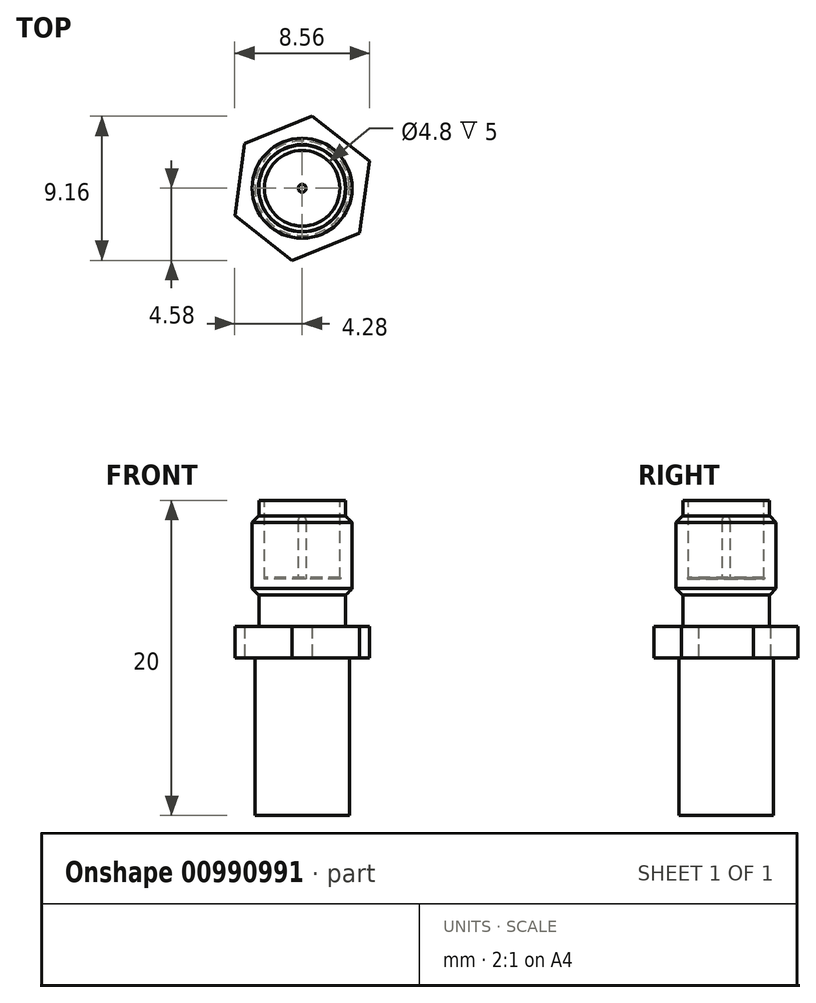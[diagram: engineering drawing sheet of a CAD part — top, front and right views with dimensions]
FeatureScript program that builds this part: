
annotation { "Feature Type Name" : "Feature", "Feature Type Description" : "" }
export const myFeature = defineFeature(function(context is Context, id is Id, definition is map)
    precondition{}
    {
        {
            var Q0;
            Q0=qCreatedBy(makeId("Top.planeOp"),FACE);
            var sketch = newSketch(context, id + "F0", { "sketchPlane" : qUnion([Q0])});
            skCircle(sketch, "E0.cCircle", {"center": v(0, 0) * mm, "radius": 4 * mm, "construction": true});
            skLineSegment(sketch, "E0.0", {"start": v(-3.65, 2.83) * mm, "end": v(0.63, 4.58) * mm});
            skLineSegment(sketch, "E0.1", {"start": v(0.63, 4.58) * mm, "end": v(4.28, 1.74) * mm});
            skLineSegment(sketch, "E0.2", {"start": v(4.28, 1.74) * mm, "end": v(3.65, -2.83) * mm});
            skLineSegment(sketch, "E0.3", {"start": v(3.65, -2.83) * mm, "end": v(-0.63, -4.58) * mm});
            skLineSegment(sketch, "E0.4", {"start": v(-0.63, -4.58) * mm, "end": v(-4.28, -1.74) * mm});
            skLineSegment(sketch, "E0.5", {"start": v(-4.28, -1.74) * mm, "end": v(-3.65, 2.83) * mm});
            skPoint(sketch, "E0.0.midPoint", {"position": v(-1.5, 3.7) * mm});
            skSolve(sketch);
        }
        {
            var Q0;
            Q0=qSketchRegion(id+"F0",true);
            extrude(context, id + "F1", {"entities" : qUnion([Q0]), "depth" : 2 * mm, "offsetDistance" : 25 * mm});
        }
        {
            var Q0;
            Q0=makeQuery(id+"F1.opExtrude","CAP_FACE",FACE,{"disambiguationData":[OSD([sQuery(id+"F0.wireOp",EDGE,"E0.0"),sQuery(id+"F0.wireOp",EDGE,"E0.1"),sQuery(id+"F0.wireOp",EDGE,"E0.2"),sQuery(id+"F0.wireOp",EDGE,"E0.3"),sQuery(id+"F0.wireOp",EDGE,"E0.4"),sQuery(id+"F0.wireOp",EDGE,"E0.5")])],"isStart":false});
            var sketch = newSketch(context, id + "F2", { "sketchPlane" : qUnion([Q0])});
            skCircle(sketch, "E1", {"center": v(0, 0) * mm, "radius": 2.75 * mm});
            skSolve(sketch);
        }
        {
            var Q0;
            Q0=qSketchRegion(id+"F2",true);
            extrude(context, id + "F3", {"entities" : qUnion([Q0]), "operationType" : NewBodyOperationType.ADD, "depth" : 2 * mm, "offsetDistance" : 25 * mm});
        }
        {
            var Q0;
            Q0=makeQuery(id+"F3.opExtrude","CAP_FACE",FACE,{"disambiguationData":[OSD([sQuery(id+"F2.wireOp",EDGE,"E1")])],"isStart":false});
            var sketch = newSketch(context, id + "F4", { "sketchPlane" : qUnion([Q0])});
            skCircle(sketch, "E2", {"center": v(0, 0) * mm, "radius": 3.17 * mm});
            skSolve(sketch);
        }
        {
            var Q0;
            Q0=qSketchRegion(id+"F4",true);
            extrude(context, id + "F5", {"entities" : qUnion([Q0]), "operationType" : NewBodyOperationType.ADD, "depth" : 5 * mm, "offsetDistance" : 25 * mm});
        }
        {
            var Q0;
            Q0=makeQuery(id+"F5.opExtrude","CAP_FACE",FACE,{"disambiguationData":[OSD([sQuery(id+"F4.wireOp",EDGE,"E2")])],"isStart":false});
            var sketch = newSketch(context, id + "F6", { "sketchPlane" : qUnion([Q0])});
            skCircle(sketch, "E3", {"center": v(0, 0) * mm, "radius": 2.75 * mm});
            skSolve(sketch);
        }
        {
            var Q0;
            Q0=qSketchRegion(id+"F6",true);
            extrude(context, id + "F7", {"entities" : qUnion([Q0]), "operationType" : NewBodyOperationType.ADD, "depth" : 1 * mm, "offsetDistance" : 25 * mm});
        }
        {
            var Q0;
            Q0=makeQuery(id+"F5.opExtrude","CAP_EDGE",EDGE,{"disambiguationData":[OSD([sQuery(id+"F4.wireOp",EDGE,"E2")])],"isStart":false});
            chamfer(context, id + "F8", {"entities" : qUnion([Q0]), "width" : .4 * mm, "tangentPropagation" : true});
        }
        {
            var Q0;
            Q0=makeQuery(id+"F5.opExtrude","CAP_EDGE",EDGE,{"disambiguationData":[OSD([sQuery(id+"F4.wireOp",EDGE,"E2")])],"isStart":true});
            chamfer(context, id + "F9", {"entities" : qUnion([Q0]), "width" : .4 * mm, "tangentPropagation" : true});
        }
        {
            var Q0;
            Q0=makeQuery(id+"F7.opExtrude","CAP_FACE",FACE,{"disambiguationData":[OSD([sQuery(id+"F6.wireOp",EDGE,"E3")])],"isStart":false});
            var sketch = newSketch(context, id + "F10", { "sketchPlane" : qUnion([Q0])});
            skCircle(sketch, "E4", {"center": v(0, 0) * mm, "radius": 2.4 * mm});
            skSolve(sketch);
        }
        {
            var Q0;
            Q0=qSketchRegion(id+"F10",true);
            extrude(context, id + "F11", {"entities" : qUnion([Q0]), "operationType" : NewBodyOperationType.REMOVE, "oppositeDirection" : true, "depth" : 5 * mm, "offsetDistance" : 25 * mm});
        }
        {
            var Q0;
            Q0=makeQuery(id+"F11.boolean.opBoolean","COPY",FACE,{"derivedFrom":makeQuery(id+"F11.opExtrude","CAP_FACE",FACE,{"disambiguationData":[OSD([sQuery(id+"F10.wireOp",EDGE,"E4")])],"isStart":false})});
            var sketch = newSketch(context, id + "F12", { "sketchPlane" : qUnion([Q0])});
            skCircle(sketch, "E5", {"center": v(0, 0) * mm, "radius": 0.25 * mm});
            skSolve(sketch);
        }
        {
            var Q0;
            Q0=qSketchRegion(id+"F12",true);
            extrude(context, id + "F13", {"entities" : qUnion([Q0]), "operationType" : NewBodyOperationType.ADD, "depth" : 4 * mm, "offsetDistance" : 25 * mm});
        }
        {
            var Q0;
            Q0=makeQuery(id+"F13.opExtrude","CAP_EDGE",EDGE,{"disambiguationData":[OSD([sQuery(id+"F12.wireOp",EDGE,"E5")])],"isStart":false});
            fillet(context, id + "F14", {"entities" : qUnion([Q0]), "radius" : .25 * mm, "tangentPropagation" : true, "allowEdgeOverflow" : false});
        }
        {
            var Q0;
            Q0=makeQuery(id+"F1.opExtrude","CAP_FACE",FACE,{"disambiguationData":[OSD([sQuery(id+"F0.wireOp",EDGE,"E0.0"),sQuery(id+"F0.wireOp",EDGE,"E0.1"),sQuery(id+"F0.wireOp",EDGE,"E0.2"),sQuery(id+"F0.wireOp",EDGE,"E0.3"),sQuery(id+"F0.wireOp",EDGE,"E0.4"),sQuery(id+"F0.wireOp",EDGE,"E0.5")])],"isStart":true});
            var sketch = newSketch(context, id + "F15", { "sketchPlane" : qUnion([Q0])});
            skCircle(sketch, "E6", {"center": v(0, 0) * mm, "radius": 3 * mm});
            skSolve(sketch);
        }
        {
            var Q0;
            Q0=qSketchRegion(id+"F15",true);
            extrude(context, id + "F16", {"entities" : qUnion([Q0]), "depth" : 10 * mm, "offsetDistance" : 25 * mm});
        }
        {
            var Q0;
            Q0=makeQuery(id+"F11.boolean.opBoolean","COPY",FACE,{"derivedFrom":makeQuery(id+"F11.opExtrude","CAP_FACE",FACE,{"disambiguationData":[OSD([sQuery(id+"F10.wireOp",EDGE,"E4")])],"isStart":false})});
            var sketch = newSketch(context, id + "F17", { "sketchPlane" : qUnion([Q0])});
            skCircle(sketch, "E7", {"center": v(0, 0) * mm, "radius": 2.44 * mm});
            skSolve(sketch);
        }
        {
            var Q0;
            Q0=qSketchRegion(id+"F17",true);
            extrude(context, id + "F18", {"entities" : qUnion([Q0]), "depth" : .1 * mm, "offsetDistance" : 25 * mm});
        }
    });
